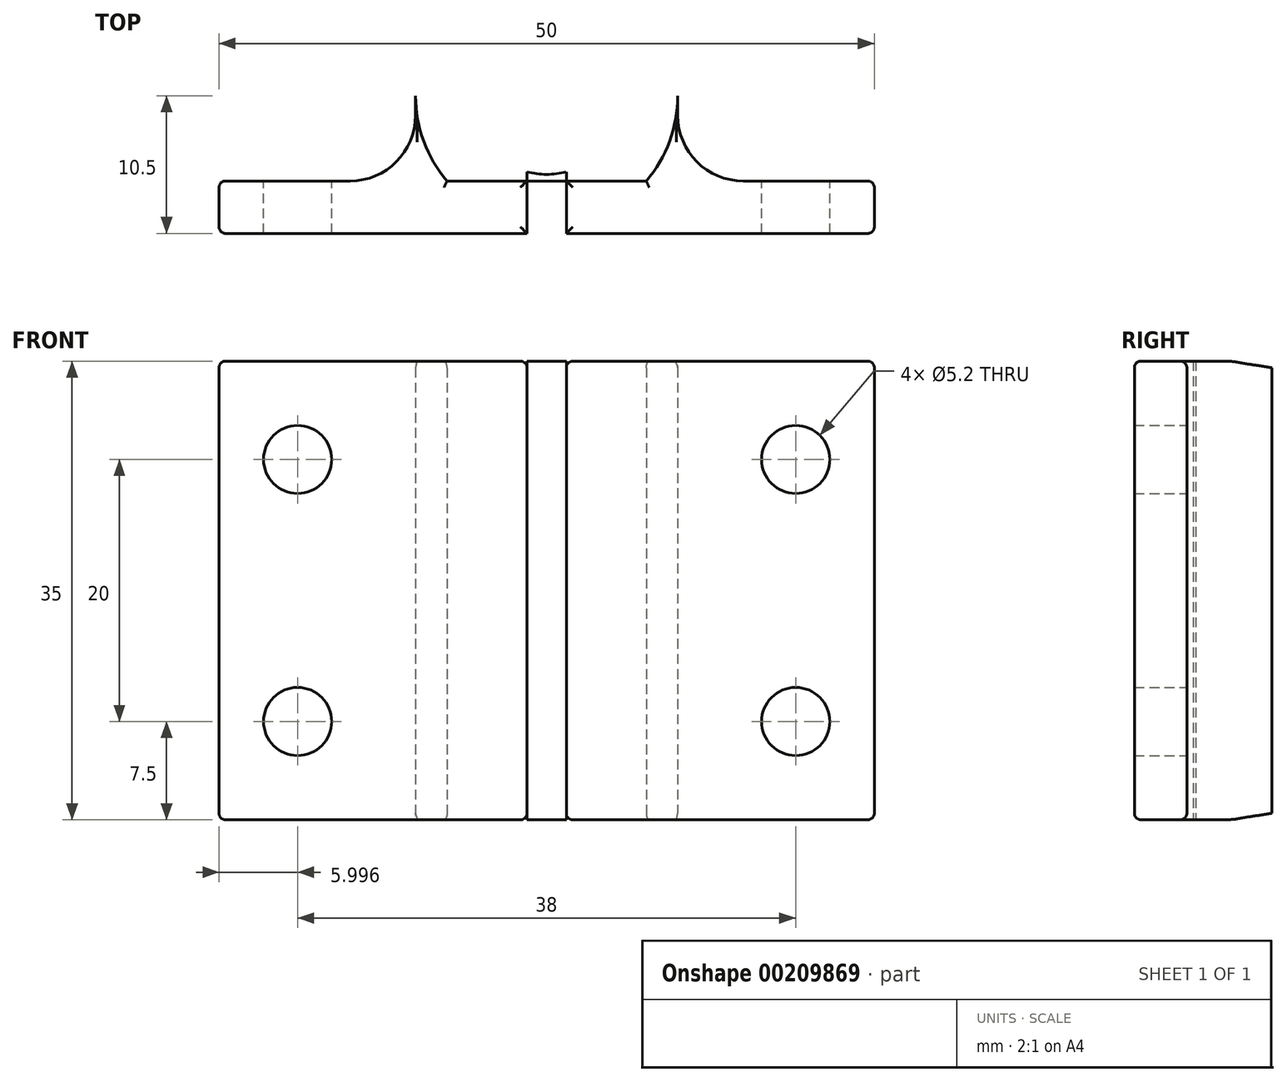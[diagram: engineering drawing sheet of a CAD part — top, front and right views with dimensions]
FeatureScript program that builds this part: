
annotation { "Feature Type Name" : "Feature", "Feature Type Description" : "" }
export const myFeature = defineFeature(function(context is Context, id is Id, definition is map)
    precondition{}
    {
        {
            var Q0;
            Q0=qCreatedBy(makeId("Top.planeOp"),FACE);
            var sketch = newSketch(context, id + "F0", { "sketchPlane" : qUnion([Q0])});
            skCircle(sketch, "E0", {"center": v(-24.33, 35.38) * mm, "radius": 6 * mm});
            skCircle(sketch, "E1", {"center": v(-24.33, 35.38) * mm, "radius": 10 * mm});
            skLineSegment(sketch, "E2", {"start": v(-24.33, 35.38) * mm, "end": v(-24.33, 24.88) * mm, "construction": true});
            skLineSegment(sketch, "E3.bottom", {"start": v(-49.33, 24.88) * mm, "end": v(0.67, 24.88) * mm});
            skLineSegment(sketch, "E3.top", {"start": v(-49.33, 28.88) * mm, "end": v(0.67, 28.88) * mm});
            skLineSegment(sketch, "E3.left", {"start": v(-49.33, 24.88) * mm, "end": v(-49.33, 28.88) * mm});
            skLineSegment(sketch, "E3.right", {"start": v(0.67, 24.88) * mm, "end": v(0.67, 28.88) * mm});
            skLineSegment(sketch, "E4", {"start": v(-34.33, 35.38) * mm, "end": v(-14.33, 35.38) * mm, "construction": true});
            skLineSegment(sketch, "E5", {"start": v(-34.33, 35.38) * mm, "end": v(-34.33, 28.88) * mm});
            skLineSegment(sketch, "E6", {"start": v(-14.33, 35.38) * mm, "end": v(-14.33, 28.88) * mm});
            skLineSegment(sketch, "E7", {"start": v(-25.83, 29.57) * mm, "end": v(-25.83, 24.88) * mm});
            skLineSegment(sketch, "E8", {"start": v(-22.83, 29.57) * mm, "end": v(-22.83, 24.88) * mm});
            skSolve(sketch);
        }
        {
            var Q0;
            {var subQ0=sQuery(id+"F0.wireOp",EDGE,"E3.top");var subQ1=sQuery(id+"F0.wireOp",EDGE,"E1");var subQ2=makeQuery(id+"F0.imprint","INTERSECT",VERTEX,{"disambiguationData":[OD(0.0)],"derivedFrom":[subQ1,subQ0]});Q0=makeQuery(id+"F0.imprint","IMPRINT",FACE,{"disambiguationData":[TD([[makeQuery(id+"F0.imprint","IMPRINT",EDGE,{"disambiguationData":[TD([[subQ2,-1.0]])],"derivedFrom":subQ1}),1.0]])]});}
            var Q1;
            {var subQ3=sQuery(id+"F0.wireOp",EDGE,"E5");Q1=makeQuery(id+"F0.imprint","IMPRINT",FACE,{"disambiguationData":[TD([[makeQuery(id+"F0.imprint","IMPRINT",EDGE,{"derivedFrom":subQ3}),1.0]])]});}
            var Q2;
            {var subQ0=sQuery(id+"F0.wireOp",EDGE,"E6");Q2=makeQuery(id+"F0.imprint","IMPRINT",FACE,{"disambiguationData":[TD([[makeQuery(id+"F0.imprint","IMPRINT",EDGE,{"derivedFrom":subQ0}),-1.0]])]});}
            var Q3;
            Q3=makeQuery(id+"F0.imprint","IMPRINT",FACE,{"disambiguationData":[TD([[makeQuery(id+"F0.imprint","IMPRINT",EDGE,{"derivedFrom":sQuery(id+"F0.wireOp",EDGE,"E0")}),-1.0]])]});
            var Q4;
            {var subQ0=sQuery(id+"F0.wireOp",EDGE,"E8");var subQ1=sQuery(id+"F0.wireOp",EDGE,"E1");var subQ2=makeQuery(id+"F0.imprint","INTERSECT",VERTEX,{"derivedFrom":[subQ1,subQ0]});Q4=makeQuery(id+"F0.imprint","IMPRINT",FACE,{"disambiguationData":[TD([[makeQuery(id+"F0.imprint","IMPRINT",EDGE,{"disambiguationData":[TD([[subQ2,-1.0]])],"derivedFrom":subQ1}),1.0]])]});}
            var Q5;
            {var subQ3=sQuery(id+"F0.wireOp",EDGE,"E3.right");Q5=makeQuery(id+"F0.imprint","IMPRINT",FACE,{"disambiguationData":[TD([[makeQuery(id+"F0.imprint","IMPRINT",EDGE,{"derivedFrom":subQ3}),1.0]])]});}
            var Q6;
            {var subQ4=sQuery(id+"F0.wireOp",EDGE,"E3.left");Q6=makeQuery(id+"F0.imprint","IMPRINT",FACE,{"disambiguationData":[TD([[makeQuery(id+"F0.imprint","IMPRINT",EDGE,{"derivedFrom":subQ4}),-1.0]])]});}
            extrude(context, id + "F1", {"entities" : qUnion([Q0, Q1, Q2, Q3, Q4, Q5, Q6]), "depth" : 35 * mm, "offsetDistance" : 25 * mm});
        }
        {
            var Q0;
            Q0=makeQuery(id+"F1.opExtrude","SWEPT_EDGE",EDGE,{"disambiguationData":[OSD([sQuery(id+"F0.wireOp",EDGE,"E3.top"),sQuery(id+"F0.wireOp",EDGE,"E5")])]});
            var Q1;
            Q1=makeQuery(id+"F1.opExtrude","SWEPT_EDGE",EDGE,{"disambiguationData":[OSD([sQuery(id+"F0.wireOp",EDGE,"E3.top"),sQuery(id+"F0.wireOp",EDGE,"E6")])]});
            fillet(context, id + "F2", {"entities" : qUnion([Q0, Q1]), "tangentPropagation" : true, "radius" : 5 * mm, "defaultsChanged" : true, "vertexSettings" : [], "allowEdgeOverflow" : false});
        }
        {
            var Q0;
            {var subQ0=sQuery(id+"F0.wireOp",EDGE,"E3.top");Q0=makeQuery(id+"F1.opExtrude","SWEPT_FACE",FACE,{"disambiguationData":[OSD([subQ0]),TDD([makeQuery(id+"F0.imprint","IMPRINT",EDGE,{"disambiguationData":[TD([[makeQuery(id+"F0.imprint","INTERSECT",VERTEX,{"derivedFrom":[subQ0,sQuery(id+"F0.wireOp",EDGE,"E3.right")]}),1.0]])],"derivedFrom":subQ0})])]});}
            var sketch = newSketch(context, id + "F3", { "sketchPlane" : qUnion([Q0])});
            skPoint(sketch, "E9", {"position": v(5.33, 27.5) * mm});
            skPoint(sketch, "E10", {"position": v(5.33, 7.5) * mm});
            skPoint(sketch, "E11", {"position": v(43.33, 27.5) * mm});
            skPoint(sketch, "E12", {"position": v(43.33, 7.5) * mm});
            skSolve(sketch);
        }
        {
            var Q0;
            Q0=sQuery(id+"F3.wireOp",VERTEX,"E9");
            var Q1;
            Q1=sQuery(id+"F3.wireOp",VERTEX,"E10");
            var Q2;
            Q2=sQuery(id+"F3.wireOp",VERTEX,"E11");
            var Q3;
            Q3=sQuery(id+"F3.wireOp",VERTEX,"E12");
            var Q4;
            Q4=makeQuery(id+"F1.opExtrude","SWEPT_BODY",BODY,{"disambiguationData":[OSD([sQuery(id+"F0.wireOp",EDGE,"E0"),sQuery(id+"F0.wireOp",EDGE,"E1"),sQuery(id+"F0.wireOp",EDGE,"E3.bottom"),sQuery(id+"F0.wireOp",EDGE,"E3.top"),sQuery(id+"F0.wireOp",EDGE,"E3.left"),sQuery(id+"F0.wireOp",EDGE,"E3.right"),sQuery(id+"F0.wireOp",EDGE,"E5"),sQuery(id+"F0.wireOp",EDGE,"E6"),sQuery(id+"F0.wireOp",EDGE,"E7"),sQuery(id+"F0.wireOp",EDGE,"E8")])]});
            hole(context, id + "F4", {"style" : HoleStyle.SIMPLE, "endStyle" : HoleEndStyle.BLIND, "holeDiameter" : 5.2 * mm, "majorDiameter" : 5 * mm, "holeDepth" : 10 * mm, "isTappedThrough" : true, "tappedDepth" : 12 * mm, "tapClearance" : 3, "locations" : qUnion([Q0, Q1, Q2, Q3]), "scope" : qUnion([Q4])});
        }
        {
            var Q0;
            Q0=makeQuery(id+"F1.opExtrude","CAP_FACE",FACE,{"disambiguationData":[OSD([sQuery(id+"F0.wireOp",EDGE,"E0"),sQuery(id+"F0.wireOp",EDGE,"E1"),sQuery(id+"F0.wireOp",EDGE,"E3.bottom"),sQuery(id+"F0.wireOp",EDGE,"E3.top"),sQuery(id+"F0.wireOp",EDGE,"E3.left"),sQuery(id+"F0.wireOp",EDGE,"E3.right"),sQuery(id+"F0.wireOp",EDGE,"E5"),sQuery(id+"F0.wireOp",EDGE,"E6"),sQuery(id+"F0.wireOp",EDGE,"E7"),sQuery(id+"F0.wireOp",EDGE,"E8")])],"isStart":true});
            var Q1;
            Q1=makeQuery(id+"F1.opExtrude","CAP_FACE",FACE,{"disambiguationData":[OSD([sQuery(id+"F0.wireOp",EDGE,"E0"),sQuery(id+"F0.wireOp",EDGE,"E1"),sQuery(id+"F0.wireOp",EDGE,"E3.bottom"),sQuery(id+"F0.wireOp",EDGE,"E3.top"),sQuery(id+"F0.wireOp",EDGE,"E3.left"),sQuery(id+"F0.wireOp",EDGE,"E3.right"),sQuery(id+"F0.wireOp",EDGE,"E5"),sQuery(id+"F0.wireOp",EDGE,"E6"),sQuery(id+"F0.wireOp",EDGE,"E7"),sQuery(id+"F0.wireOp",EDGE,"E8")])],"isStart":false});
            var Q2;
            Q2=makeQuery(id+"F1.opExtrude","SWEPT_FACE",FACE,{"disambiguationData":[OSD([sQuery(id+"F0.wireOp",EDGE,"E3.right")])]});
            var Q3;
            Q3=makeQuery(id+"F1.opExtrude","SWEPT_FACE",FACE,{"disambiguationData":[OSD([sQuery(id+"F0.wireOp",EDGE,"E3.left")])]});
            fillet(context, id + "F5", {"entities" : qUnion([Q0, Q1, Q2, Q3]), "tangentPropagation" : true, "radius" : 0.5 * mm, "defaultsChanged" : false, "vertexSettings" : [], "allowEdgeOverflow" : false});
        }
    });
